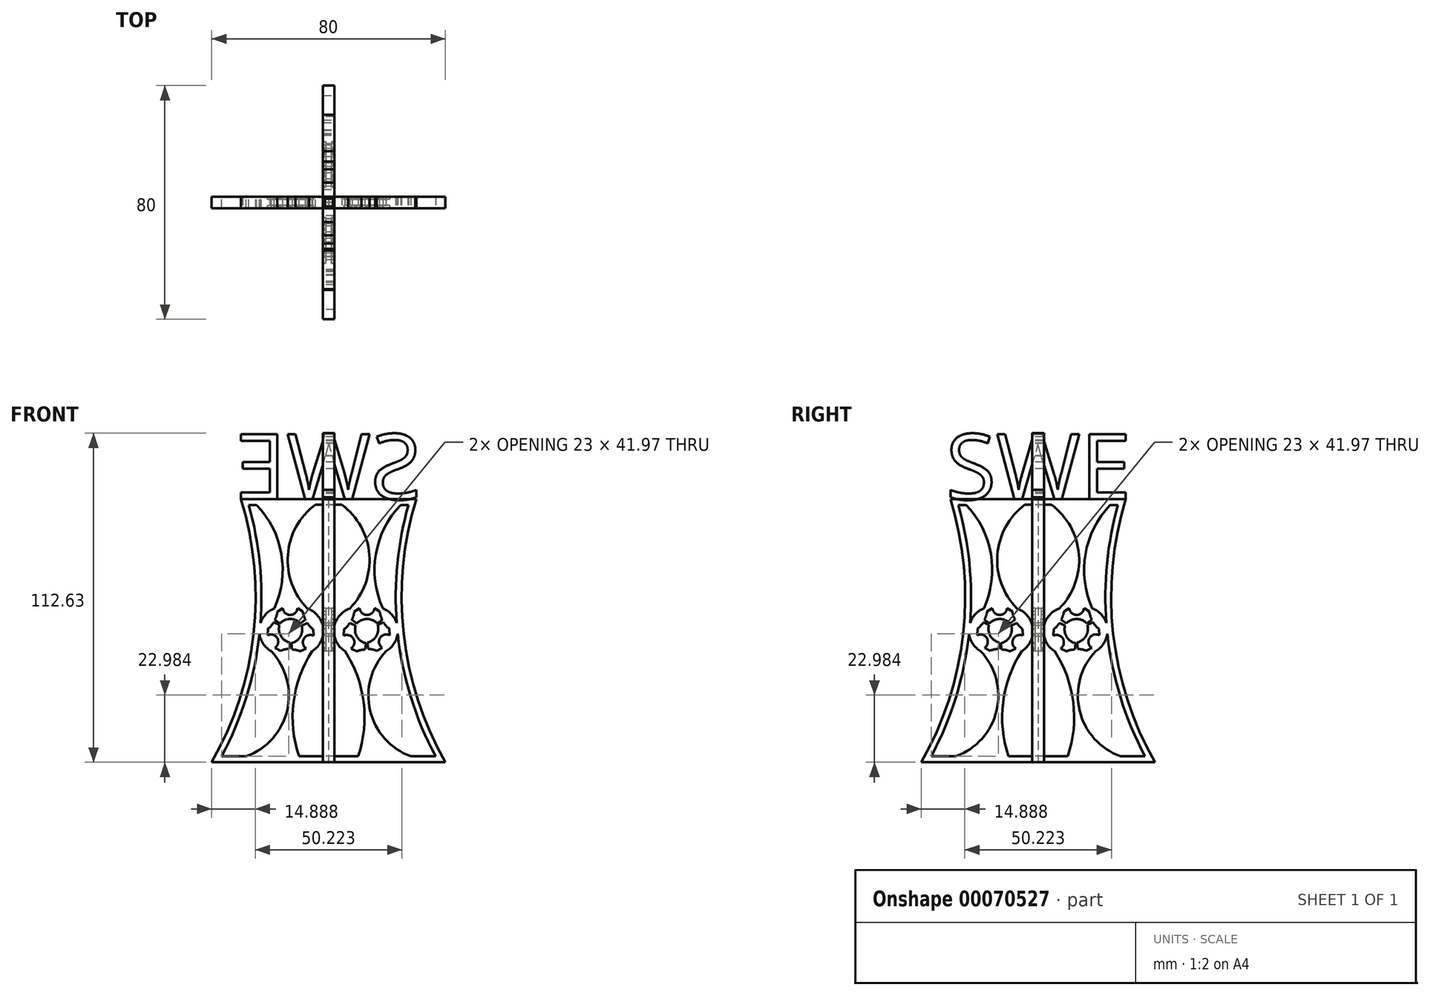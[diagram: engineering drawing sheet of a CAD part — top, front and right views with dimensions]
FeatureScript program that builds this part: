
annotation { "Feature Type Name" : "Feature", "Feature Type Description" : "" }
export const myFeature = defineFeature(function(context is Context, id is Id, definition is map)
    precondition{}
    {
        {
            var Q0;
            Q0=qCreatedBy(makeId("Right.planeOp"),FACE);
            var sketch = newSketch(context, id + "F0", { "sketchPlane" : qUnion([Q0])});
            skLineSegment(sketch, "E0", {"start": v(-30, 90) * mm, "end": v(0, 90) * mm});
            skLineSegment(sketch, "E1", {"start": v(0, 90) * mm, "end": v(0, 0) * mm});
            skLineSegment(sketch, "E2", {"start": v(0, 0) * mm, "end": v(-40, 0) * mm});
            skPoint(sketch, "E3.center", {"position": v(-13.16, 45) * mm});
            skLineSegment(sketch, "E4", {"start": v(-23.74, 45) * mm, "end": v(3.04, 45) * mm, "construction": true});
            skLineSegment(sketch, "E5", {"start": v(-13.16, 45) * mm, "end": v(0.19, 54.52) * mm, "construction": true});
            skLineSegment(sketch, "E6", {"start": v(-13.16, 45) * mm, "end": v(-2.45, 61.17) * mm, "construction": true});
            skLineSegment(sketch, "E7", {"start": v(-13.16, 45) * mm, "end": v(-8.24, 60.14) * mm, "construction": true});
            skLineSegment(sketch, "E8", {"start": v(-9.65, 47.5) * mm, "end": v(-7.9, 48.75) * mm});
            skLineSegment(sketch, "E9", {"start": v(-10.64, 52.76) * mm, "end": v(-8.82, 51.55) * mm});
            skArc(sketch, "E10", {"start": v(-8.82, 51.55) * mm, "mid": v(-8.49, 50.11) * mm, "end": v(-7.9, 48.75) * mm});
            skLineSegment(sketch, "E11", {"start": v(-13.16, 45) * mm, "end": v(-18.41, 48.75) * mm, "construction": true});
            skLineSegment(sketch, "E12", {"start": v(-13.16, 45) * mm, "end": v(-18, 52.33) * mm, "construction": true});
            skLineSegment(sketch, "E13", {"start": v(-13.16, 45) * mm, "end": v(-16.83, 56.31) * mm, "construction": true});
            skLineSegment(sketch, "E14", {"start": v(-16.66, 47.5) * mm, "end": v(-18.41, 48.75) * mm});
            skLineSegment(sketch, "E15", {"start": v(-15.68, 52.76) * mm, "end": v(-17.5, 51.55) * mm});
            skArc(sketch, "E16", {"start": v(-15.68, 52.76) * mm, "mid": v(-13.16, 50.4) * mm, "end": v(-10.64, 52.76) * mm});
            skArc(sketch, "E17", {"start": v(-18.41, 48.75) * mm, "mid": v(-17.83, 50.11) * mm, "end": v(-17.5, 51.55) * mm});
            skArc(sketch, "E18", {"start": v(-9.65, 47.5) * mm, "mid": v(-13.16, 49) * mm, "end": v(-16.66, 47.5) * mm});
            skLineSegment(sketch, "E19", {"start": v(-25.53, 52.65) * mm, "end": v(-2.82, 52.65) * mm, "construction": true});
            skLineSegment(sketch, "E20", {"start": v(-16.66, 47.5) * mm, "end": v(-2.86, 47.5) * mm, "construction": true});
            skArc(sketch, "E21.1.0", {"start": v(-18.36, 39.15) * mm, "mid": v(-17.59, 42.5) * mm, "end": v(-20.88, 43.52) * mm});
            skLineSegment(sketch, "E21.1.1", {"start": v(-18.36, 39.15) * mm, "end": v(-16.4, 38.18) * mm});
            skArc(sketch, "E21.1.2", {"start": v(-13.52, 38.78) * mm, "mid": v(-15, 38.61) * mm, "end": v(-16.4, 38.18) * mm});
            skLineSegment(sketch, "E21.1.3", {"start": v(-13.31, 40.92) * mm, "end": v(-13.52, 38.78) * mm});
            skArc(sketch, "E21.1.4", {"start": v(-16.82, 47) * mm, "mid": v(-16.37, 43.21) * mm, "end": v(-13.31, 40.92) * mm});
            skLineSegment(sketch, "E21.1.5", {"start": v(-16.82, 47) * mm, "end": v(-18.78, 47.9) * mm});
            skArc(sketch, "E21.1.6", {"start": v(-20.75, 45.7) * mm, "mid": v(-19.66, 46.7) * mm, "end": v(-18.78, 47.9) * mm});
            skLineSegment(sketch, "E21.1.7", {"start": v(-20.88, 43.52) * mm, "end": v(-20.75, 45.7) * mm});
            skArc(sketch, "E21.2.0", {"start": v(-5.18, 43.3) * mm, "mid": v(-8.47, 42.3) * mm, "end": v(-7.7, 38.94) * mm});
            skLineSegment(sketch, "E21.2.1", {"start": v(-5.18, 43.3) * mm, "end": v(-5.31, 45.48) * mm});
            skArc(sketch, "E21.2.2", {"start": v(-7.28, 47.68) * mm, "mid": v(-6.4, 46.49) * mm, "end": v(-5.31, 45.48) * mm});
            skLineSegment(sketch, "E21.2.3", {"start": v(-9.23, 46.79) * mm, "end": v(-7.28, 47.68) * mm});
            skArc(sketch, "E21.2.4", {"start": v(-12.74, 40.7) * mm, "mid": v(-9.7, 43) * mm, "end": v(-9.23, 46.79) * mm});
            skLineSegment(sketch, "E21.2.5", {"start": v(-12.74, 40.7) * mm, "end": v(-12.54, 38.57) * mm});
            skArc(sketch, "E21.2.6", {"start": v(-9.65, 37.97) * mm, "mid": v(-11.06, 38.4) * mm, "end": v(-12.54, 38.57) * mm});
            skLineSegment(sketch, "E21.2.7", {"start": v(-7.7, 38.94) * mm, "end": v(-9.65, 37.97) * mm});
            skArc(sketch, "E22", {"start": v(-40, 0) * mm, "mid": v(-25.68, 43.96) * mm, "end": v(-30, 90) * mm});
            skArc(sketch, "E23.0", {"start": v(-36.61, 2) * mm, "mid": v(-28.13, 22.37) * mm, "end": v(-23.67, 43.97) * mm});
            skLineSegment(sketch, "E23.1", {"start": v(-2, 2) * mm, "end": v(-10.14, 2) * mm});
            skLineSegment(sketch, "E23.2", {"start": v(-2, 88.16) * mm, "end": v(-2, 46.71) * mm});
            skPoint(sketch, "E24.endSnap0", {"position": v(-6.48, 49.76) * mm});
            skArc(sketch, "E25", {"start": v(-2.35, 52.7) * mm, "mid": v(-2.16, 53.2) * mm, "end": v(-2, 53.7) * mm});
            skPoint(sketch, "E26", {"position": v(-17.38, 38.66) * mm});
            skPoint(sketch, "E27.end.orphan", {"position": v(-24.47, 38.01) * mm});
            skPoint(sketch, "E24.start.orphan", {"position": v(-23.02, 53.7) * mm});
            skPoint(sketch, "E28.end.orphan", {"position": v(-21.83, 49.76) * mm});
            skPoint(sketch, "E29.start.orphan", {"position": v(-2, 38.01) * mm});
            skPoint(sketch, "E30.trimOffspring.end.orphan", {"position": v(-4.48, 40.24) * mm});
            skArc(sketch, "E31", {"start": v(-18.58, 52.65) * mm, "mid": v(-21.51, 50.66) * mm, "end": v(-23.33, 47.62) * mm});
            skArc(sketch, "E32", {"start": v(-5.63, 38) * mm, "mid": v(-3.3, 40.2) * mm, "end": v(-2, 43.13) * mm});
            skArc(sketch, "E33", {"start": v(-28.2, 2) * mm, "mid": v(-14.2, 17.7) * mm, "end": v(-19.66, 38) * mm});
            skArc(sketch, "E34", {"start": v(-5.63, 38) * mm, "mid": v(-12, 20.51) * mm, "end": v(-10.14, 2) * mm});
            skArc(sketch, "E35.trimOffspring", {"start": v(-23.33, 47.62) * mm, "mid": v(-23.55, 68.02) * mm, "end": v(-27.35, 88.07) * mm});
            skArc(sketch, "E36.trimOffspring", {"start": v(-23.67, 43.97) * mm, "mid": v(-22.36, 40.51) * mm, "end": v(-19.66, 38) * mm});
            skLineSegment(sketch, "E37.trimOffspring", {"start": v(-28.2, 2) * mm, "end": v(-36.61, 2) * mm});
            skPoint(sketch, "E38.orphan", {"position": v(-25.35, 45) * mm});
            skArc(sketch, "E39.trimOffspring", {"start": v(-2, 46.71) * mm, "mid": v(-3.87, 50.36) * mm, "end": v(-7.28, 52.65) * mm});
            skLineSegment(sketch, "E40.trimOffspring", {"start": v(-2, 43.13) * mm, "end": v(-2, 2) * mm});
            skLineSegment(sketch, "E41", {"start": v(-27.35, 88.07) * mm, "end": v(-2, 88.16) * mm});
            skArc(sketch, "E42", {"start": v(-18.58, 52.65) * mm, "mid": v(-16.18, 71.3) * mm, "end": v(-24.67, 88.08) * mm});
            skArc(sketch, "E43", {"start": v(-4.54, 88.15) * mm, "mid": v(-13.96, 71.02) * mm, "end": v(-7.28, 52.65) * mm});
            skSolve(sketch);
        }
        {
            var Q0;
            Q0=qSketchRegion(id+"F0",true);
            extrude(context, id + "F1", {"entities" : qUnion([Q0]), "depth" : 2 * mm, "hasSecondDirection" : true, "secondDirectionOppositeDirection" : true, "secondDirectionDepth" : 2 * mm});
        }
        {
            var Q0;
            Q0=qCreatedBy(makeId("Right.planeOp"),FACE);
            var sketch = newSketch(context, id + "F2", { "sketchPlane" : qUnion([Q0])});
            skLineSegment(sketch, "E44", {"start": v(0, 81) * mm, "end": v(0, -28.5) * mm, "construction": true});
            skSolve(sketch);
        }
        {
            var Q0;
            Q0=qCreatedBy(makeId("Right.planeOp"),FACE);
            var sketch = newSketch(context, id + "F3", { "sketchPlane" : qUnion([Q0])});
            skText(sketch, "E45", { "text": "SWE", "fontName": "OpenSans-Regular.ttf"});
            const initialGuessF3  = {"E45": [-0.0316, 0.09, 1, 0, 0.0225]};
            skSetInitialGuess(sketch, initialGuessF3);
            skSolve(sketch);
        }
        {
            var Q0;
            Q0=qSketchRegion(id+"F3",true);
            extrude(context, id + "F4", {"entities" : qUnion([Q0]), "depth" : 2 * mm, "hasSecondDirection" : true, "secondDirectionOppositeDirection" : true, "secondDirectionDepth" : 2 * mm});
        }
        {
            var Q0;
            Q0=qCreatedBy(makeId("Right.planeOp"),FACE);
            var sketch = newSketch(context, id + "F5", { "sketchPlane" : qUnion([Q0])});
            skLineSegment(sketch, "E46", {"start": v(0, 67.06) * mm, "end": v(0, 97.37) * mm, "construction": true});
            skSolve(sketch);
        }
        {
            var Q0;
            Q0=makeQuery(id+"F4.opExtrude","SWEPT_BODY",BODY,{"disambiguationData":[OSD([sQuery(id+"F3.wireOp",EDGE,"E45.sketch_text.stroke-45"),sQuery(id+"F3.wireOp",EDGE,"E45.sketch_text.stroke-46"),sQuery(id+"F3.wireOp",EDGE,"E45.sketch_text.stroke-47"),sQuery(id+"F3.wireOp",EDGE,"E45.sketch_text.stroke-48"),sQuery(id+"F3.wireOp",EDGE,"E45.sketch_text.stroke-49"),sQuery(id+"F3.wireOp",EDGE,"E45.sketch_text.stroke-50"),sQuery(id+"F3.wireOp",EDGE,"E45.sketch_text.stroke-51"),sQuery(id+"F3.wireOp",EDGE,"E45.sketch_text.stroke-52"),sQuery(id+"F3.wireOp",EDGE,"E45.sketch_text.stroke-53"),sQuery(id+"F3.wireOp",EDGE,"E45.sketch_text.stroke-54"),sQuery(id+"F3.wireOp",EDGE,"E45.sketch_text.stroke-55"),sQuery(id+"F3.wireOp",EDGE,"E45.sketch_text.stroke-56")])]});
            var Q1;
            Q1=makeQuery(id+"F4.opExtrude","SWEPT_BODY",BODY,{"disambiguationData":[OSD([sQuery(id+"F3.wireOp",EDGE,"E45.sketch_text.stroke-25"),sQuery(id+"F3.wireOp",EDGE,"E45.sketch_text.stroke-26"),sQuery(id+"F3.wireOp",EDGE,"E45.sketch_text.stroke-27"),sQuery(id+"F3.wireOp",EDGE,"E45.sketch_text.stroke-28"),sQuery(id+"F3.wireOp",EDGE,"E45.sketch_text.stroke-29"),sQuery(id+"F3.wireOp",EDGE,"E45.sketch_text.stroke-30"),sQuery(id+"F3.wireOp",EDGE,"E45.sketch_text.stroke-31"),sQuery(id+"F3.wireOp",EDGE,"E45.sketch_text.stroke-32"),sQuery(id+"F3.wireOp",EDGE,"E45.sketch_text.stroke-33"),sQuery(id+"F3.wireOp",EDGE,"E45.sketch_text.stroke-34"),sQuery(id+"F3.wireOp",EDGE,"E45.sketch_text.stroke-35"),sQuery(id+"F3.wireOp",EDGE,"E45.sketch_text.stroke-36"),sQuery(id+"F3.wireOp",EDGE,"E45.sketch_text.stroke-37"),sQuery(id+"F3.wireOp",EDGE,"E45.sketch_text.stroke-38"),sQuery(id+"F3.wireOp",EDGE,"E45.sketch_text.stroke-39"),sQuery(id+"F3.wireOp",EDGE,"E45.sketch_text.stroke-40"),sQuery(id+"F3.wireOp",EDGE,"E45.sketch_text.stroke-41"),sQuery(id+"F3.wireOp",EDGE,"E45.sketch_text.stroke-42"),sQuery(id+"F3.wireOp",EDGE,"E45.sketch_text.stroke-43"),sQuery(id+"F3.wireOp",EDGE,"E45.sketch_text.stroke-44")])]});
            var Q2;
            Q2=makeQuery(id+"F4.opExtrude","SWEPT_BODY",BODY,{"disambiguationData":[OSD([sQuery(id+"F3.wireOp",EDGE,"E45.sketch_text.stroke-0"),sQuery(id+"F3.wireOp",EDGE,"E45.sketch_text.stroke-1"),sQuery(id+"F3.wireOp",EDGE,"E45.sketch_text.stroke-2"),sQuery(id+"F3.wireOp",EDGE,"E45.sketch_text.stroke-3"),sQuery(id+"F3.wireOp",EDGE,"E45.sketch_text.stroke-4"),sQuery(id+"F3.wireOp",EDGE,"E45.sketch_text.stroke-5"),sQuery(id+"F3.wireOp",EDGE,"E45.sketch_text.stroke-6"),sQuery(id+"F3.wireOp",EDGE,"E45.sketch_text.stroke-7"),sQuery(id+"F3.wireOp",EDGE,"E45.sketch_text.stroke-8"),sQuery(id+"F3.wireOp",EDGE,"E45.sketch_text.stroke-9"),sQuery(id+"F3.wireOp",EDGE,"E45.sketch_text.stroke-10"),sQuery(id+"F3.wireOp",EDGE,"E45.sketch_text.stroke-11"),sQuery(id+"F3.wireOp",EDGE,"E45.sketch_text.stroke-12"),sQuery(id+"F3.wireOp",EDGE,"E45.sketch_text.stroke-13"),sQuery(id+"F3.wireOp",EDGE,"E45.sketch_text.stroke-14"),sQuery(id+"F3.wireOp",EDGE,"E45.sketch_text.stroke-15"),sQuery(id+"F3.wireOp",EDGE,"E45.sketch_text.stroke-16"),sQuery(id+"F3.wireOp",EDGE,"E45.sketch_text.stroke-17"),sQuery(id+"F3.wireOp",EDGE,"E45.sketch_text.stroke-18"),sQuery(id+"F3.wireOp",EDGE,"E45.sketch_text.stroke-19"),sQuery(id+"F3.wireOp",EDGE,"E45.sketch_text.stroke-20"),sQuery(id+"F3.wireOp",EDGE,"E45.sketch_text.stroke-21"),sQuery(id+"F3.wireOp",EDGE,"E45.sketch_text.stroke-22"),sQuery(id+"F3.wireOp",EDGE,"E45.sketch_text.stroke-23"),sQuery(id+"F3.wireOp",EDGE,"E45.sketch_text.stroke-24")])]});
            var Q3;
            Q3=sQuery(id+"F5.wireOp",EDGE,"E46");
            circularPattern(context, id + "F6", {"entities" : qUnion([Q0, Q1, Q2]), "axis" : qUnion([Q3]), "angle" : 90 * degree, "instanceCount" : 2});
        }
        {
            var Q0;
            Q0=qCreatedBy(makeId("Right.planeOp"),FACE);
            var sketch = newSketch(context, id + "F7", { "sketchPlane" : qUnion([Q0])});
            skCircle(sketch, "E47", {"center": v(-13.02, 44.84) * mm, "radius": 8.8 * mm});
            skSolve(sketch);
        }
        {
            var Q0;
            Q0 = qSketchRegion(id + "F7", true);
            extrude(context, id + "F8", {"entities" : qUnion([Q0]), "operationType" : NewBodyOperationType.ADD, "depth" : 1 * mm, "hasSecondDirection" : true, "secondDirectionOppositeDirection" : true, "secondDirectionDepth" : 1 * mm});
        }
        {
            var Q0;
            Q0=makeQuery(id+"F1.opExtrude","SWEPT_BODY",BODY,{"disambiguationData":[OSD([sQuery(id+"F0.wireOp",EDGE,"E0"),sQuery(id+"F0.wireOp",EDGE,"E1"),sQuery(id+"F0.wireOp",EDGE,"N8EfN9Iy-VFxy-i62X-S3Tn-et34u0hB6ofw"),sQuery(id+"F0.wireOp",EDGE,"ofOerVMI-8AtS-AqWo-Xm8z-ZVAlB3EUovam"),sQuery(id+"F0.wireOp",EDGE,"ba3e6201-bb00-4176-be12-0bcf97df4df2"),sQuery(id+"F0.wireOp",EDGE,"k6Ju8hmT-RXya-gFIe-6RDm-fDKX84Fwp2G4"),sQuery(id+"F0.wireOp",EDGE,"dTDJtstR-zKxY-rc8w-sIGn-4ASnDpw26A23"),sQuery(id+"F0.wireOp",EDGE,"Cvr0LfUC-tO0D-IxcI-B5Ti-WW2sAGeSHFF8"),sQuery(id+"F0.wireOp",EDGE,"DwRJblST-1CEV-pcTT-NFQT-YytcCcE5cTGx"),sQuery(id+"F0.wireOp",EDGE,"973229ff-babc-457a-ac66-6eeaf75bea45")])]});
            var Q1;
            Q1=sQuery(id+"F2.wireOp",EDGE,"E44");
            circularPattern(context, id + "F9", {"entities" : qUnion([Q0]), "axis" : qUnion([Q1]), "angle" : 90 * degree, "instanceCount" : round(4)});
        }
    });
